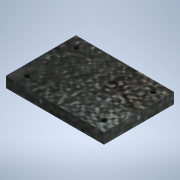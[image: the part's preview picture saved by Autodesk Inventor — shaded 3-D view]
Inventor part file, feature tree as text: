
AUTODESK INVENTOR PART (.ipt)
format: ipt  version: 2021 (Build 250183000, 183)  size: 133,632 bytes
history: native  units: mm
features: sketch x1, extrude x1, hole x1
ambient origin geometry x8: Origin, YZ Plane, XZ Plane, XY Plane, X Axis, Y Axis, Z Axis, Center Point
bodies: Solid1 (feature_tree)
feature tree (3):
  sketch  "Sketch1"  dims[d0=28.0mm d1=20.0mm d2=3.0mm d3=3.0mm d4=22.0mm d5=14.0mm d6=3.0mm d7=0.0mm d8=1.4mm d9=6.0mm d10=3.0mm d11=2.0mm d12=90.0deg d13=3.0mm d14=20.594885mm]
  extrude  "Extrusion1"  Depth=20.0mm
  hole  "Hole1"  [1 undecoded]
note: 1 required parameter value undecoded (feature->parameter linkage not recoverable at this tier; creation-order binding heuristic only, values carry confidence <= 0.55)
